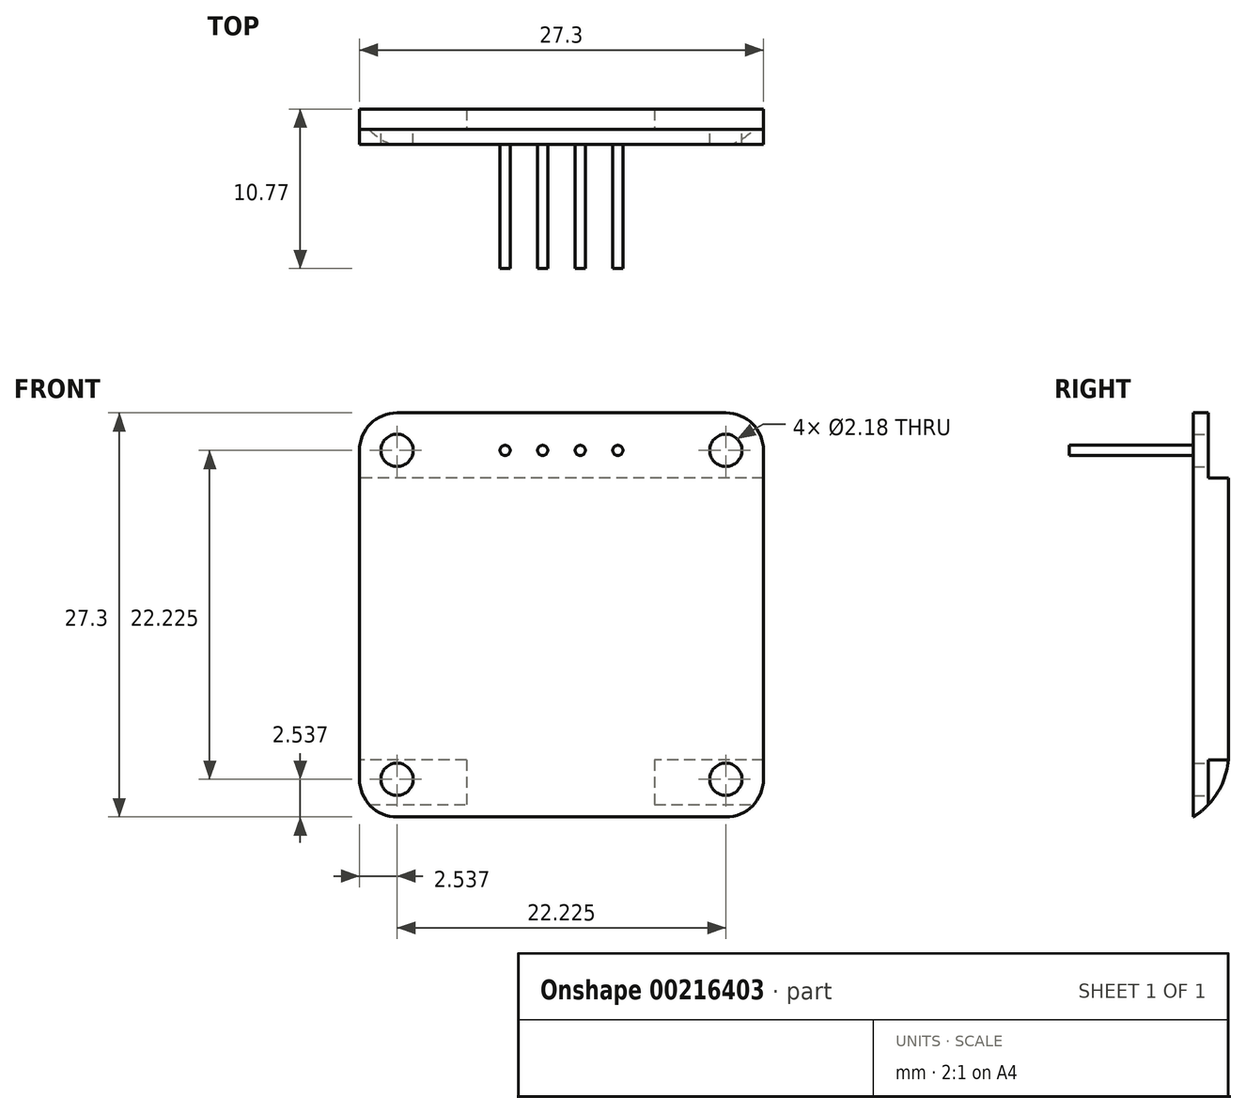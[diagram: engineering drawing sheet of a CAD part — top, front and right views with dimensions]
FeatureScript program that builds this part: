
annotation { "Feature Type Name" : "Feature", "Feature Type Description" : "" }
export const myFeature = defineFeature(function(context is Context, id is Id, definition is map)
    precondition{}
    {
        {
            var Q0;
            Q0=qCreatedBy(makeId("Front.planeOp"),FACE);
            var sketch = newSketch(context, id + "F0", { "sketchPlane" : qUnion([Q0])});
            skLineSegment(sketch, "E0.bottom", {"start": v(-11.11, 13.65) * mm, "end": v(11.11, 13.65) * mm});
            skLineSegment(sketch, "E0.top", {"start": v(-11.11, -13.65) * mm, "end": v(11.11, -13.65) * mm});
            skLineSegment(sketch, "E0.left", {"start": v(-13.65, 11.11) * mm, "end": v(-13.65, -11.11) * mm});
            skLineSegment(sketch, "E0.right", {"start": v(13.65, 11.11) * mm, "end": v(13.65, -11.11) * mm});
            skPoint(sketch, "E0.middle", {"position": v(0, 0) * mm});
            skPoint(sketch, "E1.visualSharp", {"position": v(13.65, 13.65) * mm});
            skArc(sketch, "E1.filletArc", {"start": v(13.65, 11.11) * mm, "mid": v(12.9, 12.9) * mm, "end": v(11.11, 13.65) * mm});
            skPoint(sketch, "E2.visualSharp", {"position": v(-13.65, 13.65) * mm});
            skArc(sketch, "E2.filletArc", {"start": v(-11.11, 13.65) * mm, "mid": v(-12.9, 12.9) * mm, "end": v(-13.65, 11.11) * mm});
            skPoint(sketch, "E3.visualSharp", {"position": v(-13.65, -13.65) * mm});
            skArc(sketch, "E3.filletArc", {"start": v(-13.65, -11.11) * mm, "mid": v(-12.9, -12.9) * mm, "end": v(-11.11, -13.65) * mm});
            skPoint(sketch, "E4.visualSharp", {"position": v(13.65, -13.65) * mm});
            skArc(sketch, "E4.filletArc", {"start": v(11.11, -13.65) * mm, "mid": v(12.9, -12.9) * mm, "end": v(13.65, -11.11) * mm});
            skCircle(sketch, "E5", {"center": v(-11.11, 11.11) * mm, "radius": 1.1 * mm});
            skCircle(sketch, "E6", {"center": v(11.11, 11.11) * mm, "radius": 1.1 * mm});
            skCircle(sketch, "E7", {"center": v(11.11, -11.11) * mm, "radius": 1.1 * mm});
            skCircle(sketch, "E8", {"center": v(-11.11, -11.11) * mm, "radius": 1.1 * mm});
            skSolve(sketch);
        }
        {
            var Q0;
            Q0 = qSketchRegion(id + "F0", true);
            extrude(context, id + "F1", {"entities" : qUnion([Q0]), "depth" : 1.02 * mm});
        }
        {
            var Q0;
            Q0=makeQuery(id+"F1.opExtrude","CAP_FACE",FACE,{"disambiguationData":[OSD([sQuery(id+"F0.wireOp",EDGE,"E0.bottom"),sQuery(id+"F0.wireOp",EDGE,"E0.top"),sQuery(id+"F0.wireOp",EDGE,"E0.left"),sQuery(id+"F0.wireOp",EDGE,"E0.right"),sQuery(id+"F0.wireOp",EDGE,"E1.filletArc"),sQuery(id+"F0.wireOp",EDGE,"E2.filletArc"),sQuery(id+"F0.wireOp",EDGE,"E3.filletArc"),sQuery(id+"F0.wireOp",EDGE,"E4.filletArc"),sQuery(id+"F0.wireOp",EDGE,"E5"),sQuery(id+"F0.wireOp",EDGE,"E6"),sQuery(id+"F0.wireOp",EDGE,"E7"),sQuery(id+"F0.wireOp",EDGE,"E8")])],"isStart":false});
            var sketch = newSketch(context, id + "F2", { "sketchPlane" : qUnion([Q0])});
            skCircle(sketch, "E9", {"center": v(-3.81, 11.11) * mm, "radius": 0.34 * mm});
            skCircle(sketch, "E10", {"center": v(-1.27, 11.11) * mm, "radius": 0.34 * mm});
            skCircle(sketch, "E11", {"center": v(3.81, 11.11) * mm, "radius": 0.34 * mm});
            skCircle(sketch, "E12", {"center": v(1.27, 11.11) * mm, "radius": 0.34 * mm});
            skPoint(sketch, "E13", {"position": v(-11.11, 11.11) * mm});
            skSolve(sketch);
        }
        {
            var Q0;
            Q0 = qSketchRegion(id + "F2", true);
            extrude(context, id + "F3", {"entities" : qUnion([Q0]), "operationType" : NewBodyOperationType.ADD, "depth" : 8.38 * mm});
        }
        {
            var Q0;
            Q0=makeQuery(id+"F1.opExtrude","CAP_FACE",FACE,{"disambiguationData":[OSD([sQuery(id+"F0.wireOp",EDGE,"E0.bottom"),sQuery(id+"F0.wireOp",EDGE,"E0.top"),sQuery(id+"F0.wireOp",EDGE,"E0.left"),sQuery(id+"F0.wireOp",EDGE,"E0.right"),sQuery(id+"F0.wireOp",EDGE,"E1.filletArc"),sQuery(id+"F0.wireOp",EDGE,"E2.filletArc"),sQuery(id+"F0.wireOp",EDGE,"E3.filletArc"),sQuery(id+"F0.wireOp",EDGE,"E4.filletArc"),sQuery(id+"F0.wireOp",EDGE,"E5"),sQuery(id+"F0.wireOp",EDGE,"E6"),sQuery(id+"F0.wireOp",EDGE,"E7"),sQuery(id+"F0.wireOp",EDGE,"E8")])],"isStart":true});
            var sketch = newSketch(context, id + "F4", { "sketchPlane" : qUnion([Q0])});
            skLineSegment(sketch, "E14.bottom", {"start": v(-13.65, 9.26) * mm, "end": v(13.65, 9.26) * mm});
            skLineSegment(sketch, "E14.top", {"start": v(-13.65, -9.8) * mm, "end": v(13.65, -9.8) * mm});
            skLineSegment(sketch, "E14.left", {"start": v(-13.65, 9.26) * mm, "end": v(-13.65, -9.8) * mm});
            skLineSegment(sketch, "E14.right", {"start": v(13.65, 9.26) * mm, "end": v(13.65, -9.8) * mm});
            skSolve(sketch);
        }
        {
            var Q0;
            Q0 = qSketchRegion(id + "F4", true);
            extrude(context, id + "F5", {"entities" : qUnion([Q0]), "operationType" : NewBodyOperationType.ADD, "depth" : 1.37 * mm});
        }
        {
            var Q0;
            {var subQ0=sQuery(id+"F0.wireOp",EDGE,"E0.right");var subQ1=sQuery(id+"F0.wireOp",EDGE,"E7");var subQ2=sQuery(id+"F0.wireOp",EDGE,"E0.left");var subQ3=sQuery(id+"F0.wireOp",EDGE,"E3.filletArc");var subQ4=sQuery(id+"F0.wireOp",EDGE,"E0.top");var subQ5=sQuery(id+"F0.wireOp",EDGE,"E4.filletArc");var subQ6=sQuery(id+"F0.wireOp",EDGE,"E8");Q0=makeQuery(id+"F5.boolean.opBoolean","SPLIT",FACE,{"disambiguationData":[TD([makeQuery(id+"F1.opExtrude","SWEPT_FACE",FACE,{"disambiguationData":[OSD([subQ4])]})])],"derivedFrom":makeQuery(id+"F1.opExtrude","CAP_FACE",FACE,{"disambiguationData":[OSD([sQuery(id+"F0.wireOp",EDGE,"E0.bottom"),subQ4,subQ2,subQ0,sQuery(id+"F0.wireOp",EDGE,"E1.filletArc"),sQuery(id+"F0.wireOp",EDGE,"E2.filletArc"),subQ3,subQ5,sQuery(id+"F0.wireOp",EDGE,"E5"),sQuery(id+"F0.wireOp",EDGE,"E6"),subQ1,subQ6])],"isStart":true})});}
            var sketch = newSketch(context, id + "F6", { "sketchPlane" : qUnion([Q0])});
            skLineSegment(sketch, "E15.bottom", {"start": v(-6.29, -9.8) * mm, "end": v(6.41, -9.8) * mm});
            skLineSegment(sketch, "E15.top", {"start": v(-6.29, -13.65) * mm, "end": v(6.41, -13.65) * mm});
            skLineSegment(sketch, "E15.left", {"start": v(-6.29, -9.8) * mm, "end": v(-6.29, -13.65) * mm});
            skLineSegment(sketch, "E15.right", {"start": v(6.41, -9.8) * mm, "end": v(6.41, -13.65) * mm});
            skSolve(sketch);
        }
        {
            var Q0;
            Q0 = qSketchRegion(id + "F6", true);
            var Q1;
            Q1=makeQuery(id+"F5.opExtrude","CAP_FACE",FACE,{"disambiguationData":[OSD([sQuery(id+"F4.wireOp",EDGE,"E14.bottom"),sQuery(id+"F4.wireOp",EDGE,"E14.top"),sQuery(id+"F4.wireOp",EDGE,"E14.left"),sQuery(id+"F4.wireOp",EDGE,"E14.right")])],"isStart":false});
            extrude(context, id + "F7", {"entities" : qUnion([Q0]), "operationType" : NewBodyOperationType.ADD, "endBound" : BoundingType.UP_TO_SURFACE, "endBoundEntityFace" : qUnion([Q1]), "depth" : 25.4 * mm});
        }
        {
            var Q0;
            Q0=makeQuery(id+"F7.opExtrude","CAP_EDGE",EDGE,{"disambiguationData":[OSD([sQuery(id+"F6.wireOp",EDGE,"E15.top")])],"isStart":false});
            fillet(context, id + "F8", {"entities" : qUnion([Q0]), "radius" : 5.08 * mm, "tangentPropagation" : true, "allowEdgeOverflow" : false});
        }
    });
